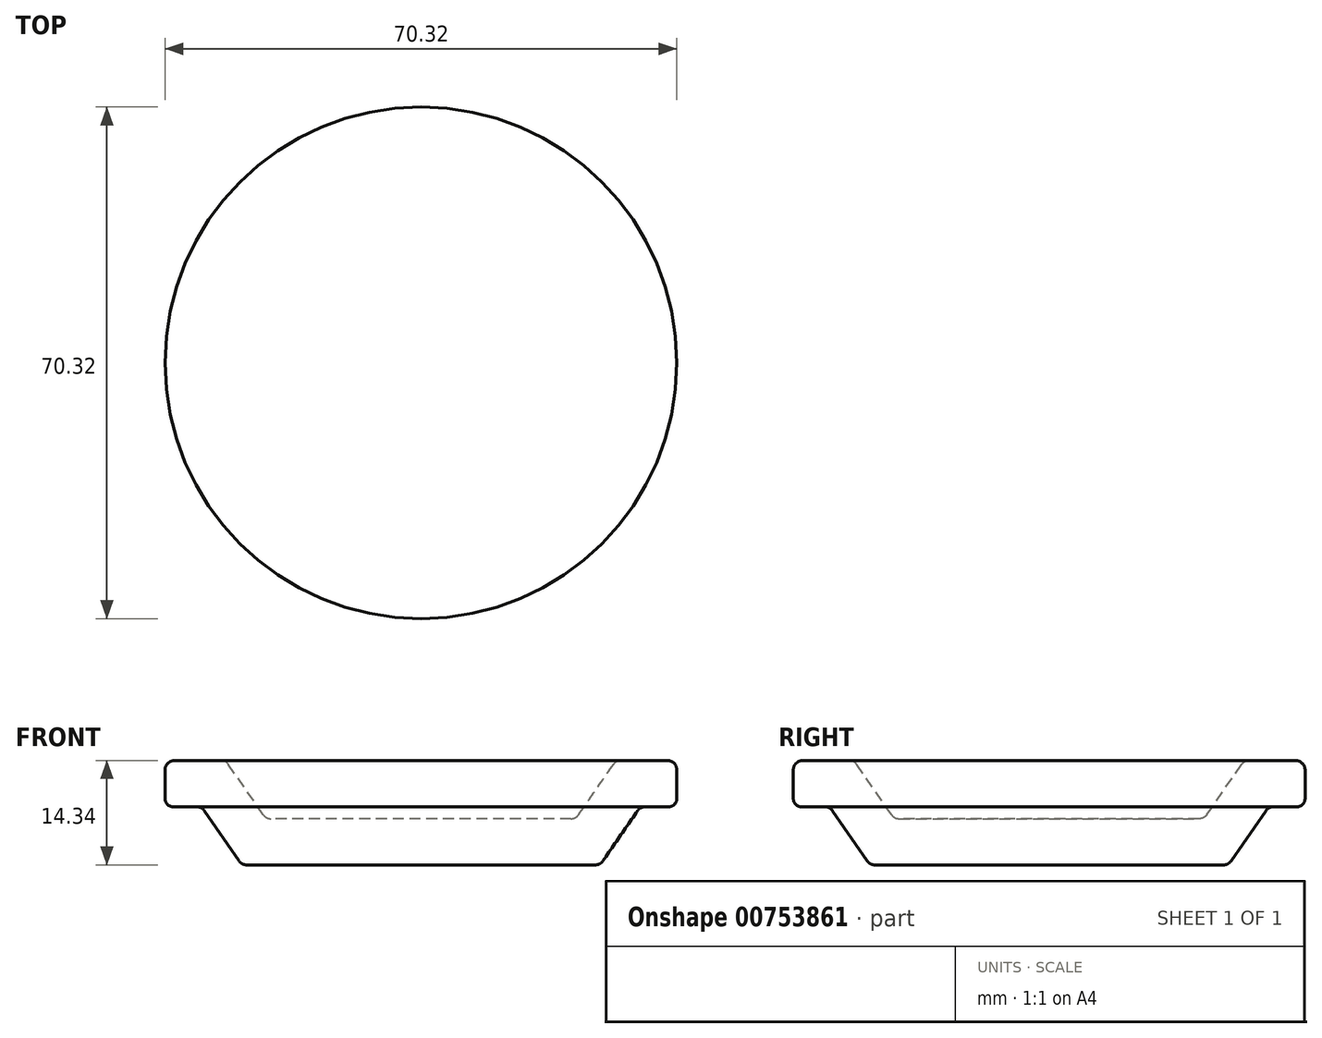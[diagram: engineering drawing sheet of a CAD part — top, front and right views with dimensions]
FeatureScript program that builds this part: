
annotation { "Feature Type Name" : "Feature", "Feature Type Description" : "" }
export const myFeature = defineFeature(function(context is Context, id is Id, definition is map)
    precondition{}
    {
        {
            var Q0;
            Q0=qCreatedBy(makeId("Front.planeOp"),FACE);
            var sketch = newSketch(context, id + "F0", { "sketchPlane" : qUnion([Q0])});
            skLineSegment(sketch, "E0", {"start": v(0, 0) * mm, "end": v(-23.96, 0) * mm});
            skLineSegment(sketch, "E1", {"start": v(-25, 0.55) * mm, "end": v(-29.76, 7.44) * mm});
            skLineSegment(sketch, "E2", {"start": v(-30.8, 7.99) * mm, "end": v(-34.05, 7.99) * mm});
            skLineSegment(sketch, "E3.0", {"start": v(-27.48, 14.34) * mm, "end": v(-33.89, 14.34) * mm});
            skLineSegment(sketch, "E3.1", {"start": v(-21.67, 6.9) * mm, "end": v(-26.43, 13.79) * mm});
            skLineSegment(sketch, "E3.2", {"start": v(0, 6.35) * mm, "end": v(-20.63, 6.35) * mm});
            skLineSegment(sketch, "E4", {"start": v(-35.16, 13.07) * mm, "end": v(-35.16, 9.1) * mm});
            skLineSegment(sketch, "E5", {"start": v(0, 0) * mm, "end": v(0, 6.35) * mm});
            skPoint(sketch, "E6.visualSharp", {"position": v(-35.16, 7.99) * mm});
            skArc(sketch, "E6.filletArc", {"start": v(-35.16, 9.1) * mm, "mid": v(-34.83, 8.31) * mm, "end": v(-34.05, 7.99) * mm});
            skPoint(sketch, "E7.visualSharp", {"position": v(-35.16, 14.34) * mm});
            skArc(sketch, "E7.filletArc", {"start": v(-33.89, 14.34) * mm, "mid": v(-34.78, 13.96) * mm, "end": v(-35.16, 13.07) * mm});
            skPoint(sketch, "E8.visualSharp", {"position": v(-26.81, 14.34) * mm});
            skArc(sketch, "E8.filletArc", {"start": v(-26.43, 13.79) * mm, "mid": v(-26.89, 14.2) * mm, "end": v(-27.48, 14.34) * mm});
            skPoint(sketch, "E9.visualSharp", {"position": v(-30.14, 7.99) * mm});
            skArc(sketch, "E9.filletArc", {"start": v(-29.76, 7.44) * mm, "mid": v(-30.22, 7.84) * mm, "end": v(-30.8, 7.99) * mm});
            skPoint(sketch, "E10.visualSharp", {"position": v(-21.3, 6.35) * mm});
            skArc(sketch, "E10.filletArc", {"start": v(-21.67, 6.9) * mm, "mid": v(-21.22, 6.5) * mm, "end": v(-20.63, 6.35) * mm});
            skPoint(sketch, "E11.visualSharp", {"position": v(-24.63, 0) * mm});
            skArc(sketch, "E11.filletArc", {"start": v(-25, 0.55) * mm, "mid": v(-24.55, 0.15) * mm, "end": v(-23.96, 0) * mm});
            skSolve(sketch);
        }
        {
            var Q0;
            Q0 = qSketchRegion(id + "F0", true);
            var Q1;
            Q1=sQuery(id+"F0.wireOp",EDGE,"E1");
            var Q2;
            Q2=sQuery(id+"F0.wireOp",EDGE,"E4");
            var Q3;
            Q3=sQuery(id+"F0.wireOp",EDGE,"E3.2");
            var Q4;
            Q4=sQuery(id+"F0.wireOp",EDGE,"E2");
            var Q5;
            Q5=sQuery(id+"F0.wireOp",EDGE,"E6.filletArc");
            var Q6;
            Q6=sQuery(id+"F0.wireOp",EDGE,"E7.filletArc");
            var Q7;
            Q7=sQuery(id+"F0.wireOp",EDGE,"E9.filletArc");
            var Q8;
            Q8=sQuery(id+"F0.wireOp",EDGE,"E11.filletArc");
            var Q9;
            Q9=sQuery(id+"F0.wireOp",EDGE,"E8.filletArc");
            var Q10;
            Q10=sQuery(id+"F0.wireOp",EDGE,"E10.filletArc");
            var Q11;
            Q11=sQuery(id+"F0.wireOp",EDGE,"E5");
            revolve(context, id + "F1", {"surfaceOperationType" : NewSurfaceOperationType.NEW, "entities" : qUnion([Q0]), "surfaceEntities" : qUnion([Q1, Q2, Q3, Q4, Q5, Q6, Q7, Q8, Q9, Q10]), "axis" : qUnion([Q11]), "revolveType" : RevolveType.FULL, "oppositeDirection" : true});
        }
    });
